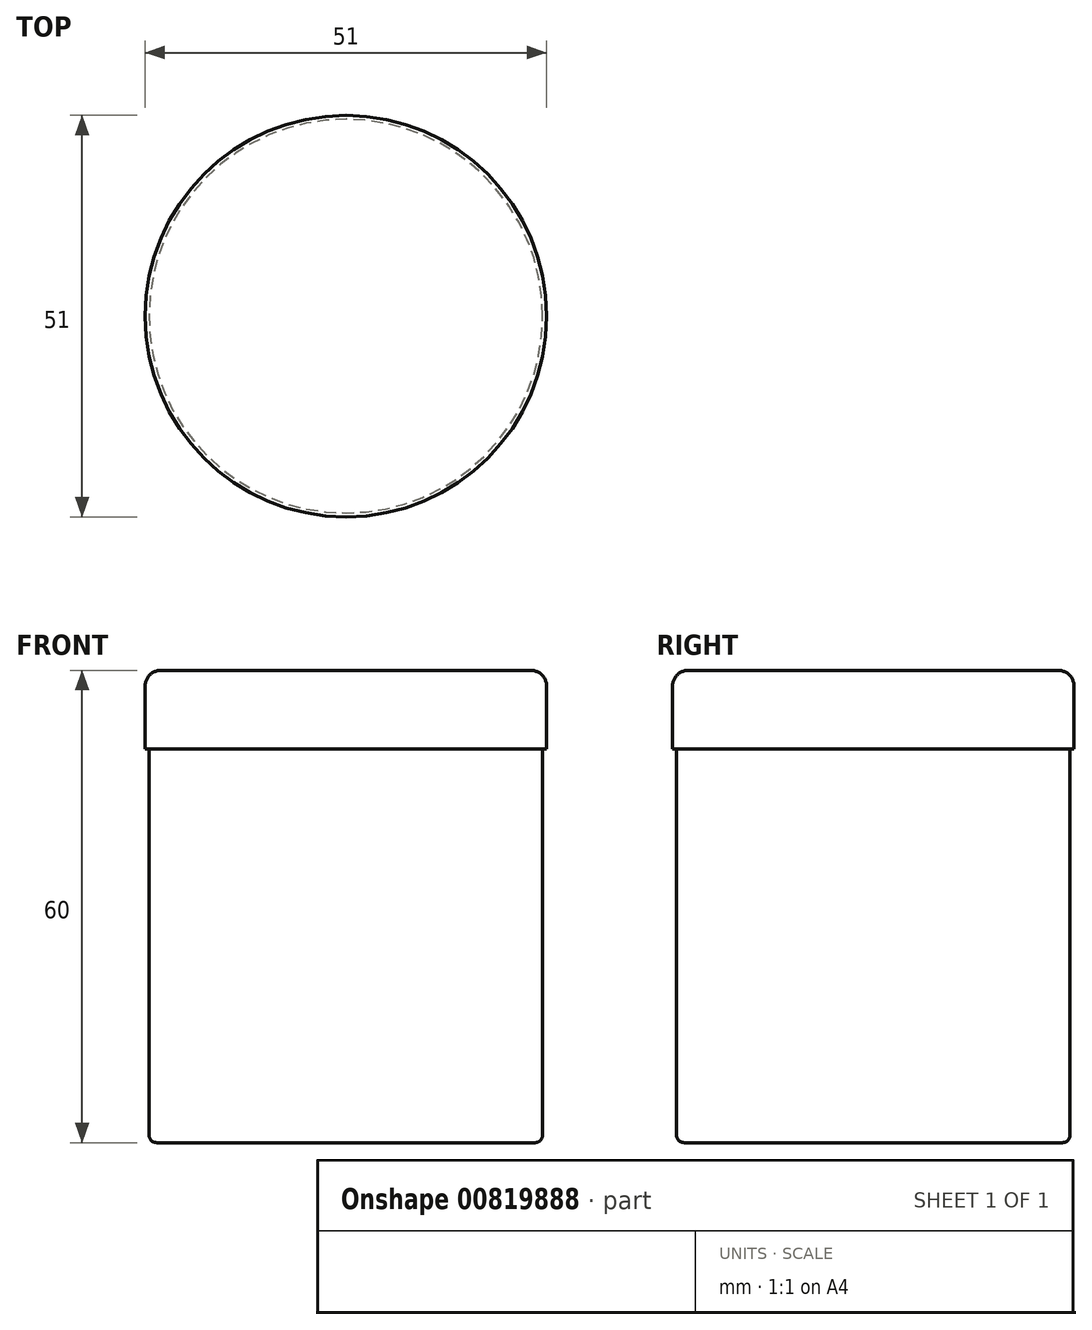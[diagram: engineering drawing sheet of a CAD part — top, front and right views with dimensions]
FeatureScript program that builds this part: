
annotation { "Feature Type Name" : "Feature", "Feature Type Description" : "" }
export const myFeature = defineFeature(function(context is Context, id is Id, definition is map)
    precondition{}
    {
        {
            var Q0;
            Q0=qCreatedBy(makeId("Top.planeOp"),FACE);
            var sketch = newSketch(context, id + "F0", { "sketchPlane" : qUnion([Q0])});
            skCircle(sketch, "E0", {"center": v(0, 0) * mm, "radius": 25 * mm});
            skSolve(sketch);
        }
        {
            var Q0;
            Q0 = qSketchRegion(id + "F0", true);
            extrude(context, id + "F1", {"entities" : qUnion([Q0]), "depth" : 50 * mm, "offsetDistance" : 25 * mm});
        }
        {
            var Q0;
            Q0=makeQuery(id+"F1.opExtrude","CAP_FACE",FACE,{"disambiguationData":[OSD([sQuery(id+"F0.wireOp",EDGE,"E0")])],"isStart":false});
            var sketch = newSketch(context, id + "F2", { "sketchPlane" : qUnion([Q0])});
            skCircle(sketch, "E1", {"center": v(0, 0) * mm, "radius": 25.5 * mm});
            skSolve(sketch);
        }
        {
            var Q0;
            Q0 = qSketchRegion(id + "F2", true);
            extrude(context, id + "F3", {"entities" : qUnion([Q0]), "operationType" : NewBodyOperationType.ADD, "depth" : 10 * mm, "offsetDistance" : 25 * mm});
        }
        {
            var Q0;
            Q0=makeQuery(id+"F3.opExtrude","CAP_EDGE",EDGE,{"disambiguationData":[OSD([sQuery(id+"F2.wireOp",EDGE,"E1")])],"isStart":false});
            fillet(context, id + "F4", {"entities" : qUnion([Q0]), "radius" : 2 * mm, "tangentPropagation" : true, "allowEdgeOverflow" : false});
        }
        {
            var Q0;
            Q0=makeQuery(id+"F1.opExtrude","CAP_EDGE",EDGE,{"disambiguationData":[OSD([sQuery(id+"F0.wireOp",EDGE,"E0")])],"isStart":true});
            fillet(context, id + "F5", {"entities" : qUnion([Q0]), "radius" : 1 * mm, "tangentPropagation" : true, "allowEdgeOverflow" : false});
        }
    });
